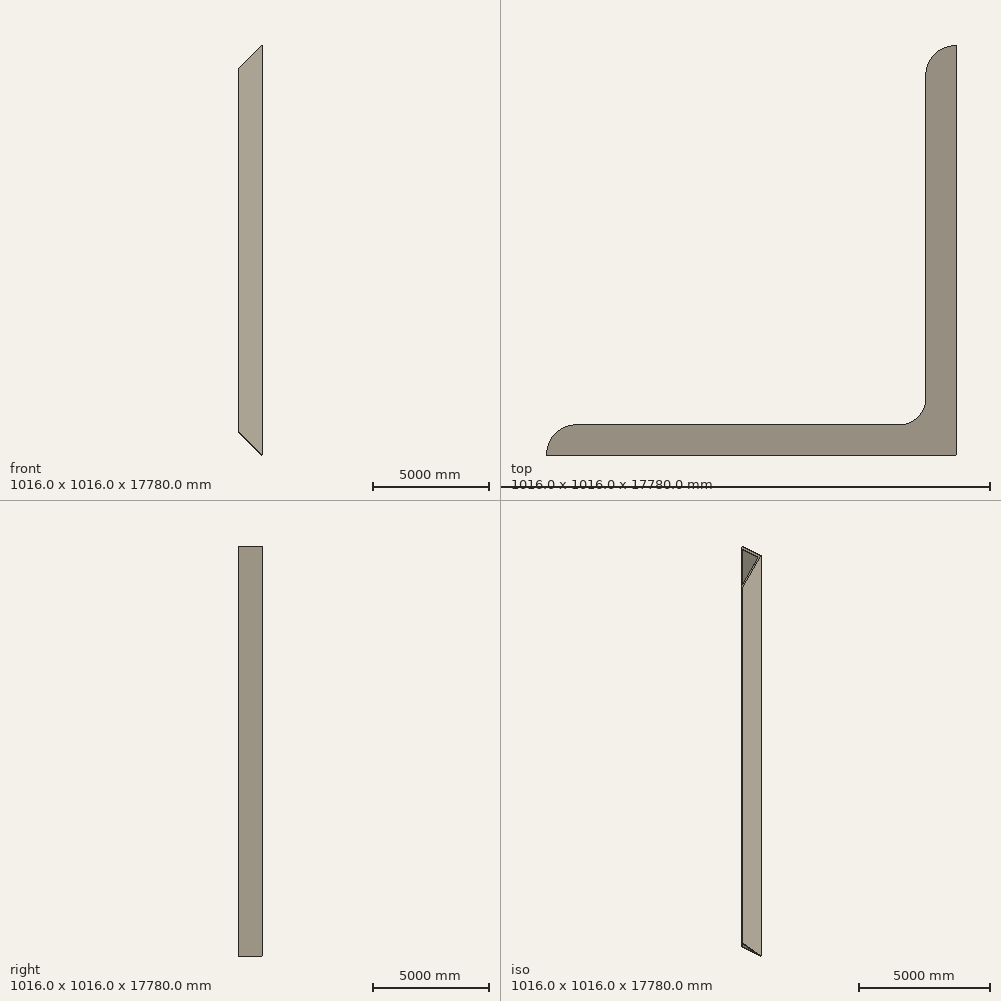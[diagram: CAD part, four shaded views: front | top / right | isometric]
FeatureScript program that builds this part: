
annotation { "Feature Type Name" : "Feature", "Feature Type Description" : "" }
export const myFeature = defineFeature(function(context is Context, id is Id, definition is map)
    precondition{}
    {
        {
            var Q0;
            Q0=qCreatedBy(makeId("Top.planeOp"),FACE);
            var sketch = newSketch(context, id + "F0", { "sketchPlane" : qUnion([Q0])});
            skLineSegment(sketch, "E0", {"start": v(0, 0) * mm, "end": v(1016, 0) * mm});
            skLineSegment(sketch, "E1", {"start": v(1016, 0) * mm, "end": v(1016, 1016) * mm});
            skLineSegment(sketch, "E2", {"start": v(939.8, 939.8) * mm, "end": v(939.8, 139.7) * mm});
            skLineSegment(sketch, "E3", {"start": v(876.3, 76.2) * mm, "end": v(76.2, 76.2) * mm});
            skArc(sketch, "E4", {"start": v(0, 0) * mm, "mid": v(22.32, 53.88) * mm, "end": v(76.2, 76.2) * mm});
            skArc(sketch, "E5", {"start": v(939.8, 939.8) * mm, "mid": v(962.12, 993.68) * mm, "end": v(1016, 1016) * mm});
            skPoint(sketch, "E6.visualSharp", {"position": v(939.8, 76.2) * mm});
            skArc(sketch, "E6.filletArc", {"start": v(876.3, 76.2) * mm, "mid": v(921.2, 94.8) * mm, "end": v(939.8, 139.7) * mm});
            skSolve(sketch);
        }
        {
            var Q0;
            Q0 = qSketchRegion(id + "F0", true);
            extrude(context, id + "F1", {"entities" : qUnion([Q0]), "depth" : 17780 * mm, "offsetDistance" : 25.4 * mm});
        }
        {
            var Q0;
            Q0=makeQuery(id+"F1.opExtrude","SWEPT_FACE",FACE,{"disambiguationData":[OSD([sQuery(id+"F0.wireOp",EDGE,"E0")])]});
            var sketch = newSketch(context, id + "F2", { "sketchPlane" : qUnion([Q0])});
            skLineSegment(sketch, "E7", {"start": v(1016, 17780) * mm, "end": v(-530.7, 16233.3) * mm});
            skLineSegment(sketch, "E8", {"start": v(-530.7, 16233.3) * mm, "end": v(-822.01, 18363) * mm});
            skLineSegment(sketch, "E9", {"start": v(-822.01, 18363) * mm, "end": v(1016, 17780) * mm});
            skLineSegment(sketch, "E10", {"start": v(1016, 0) * mm, "end": v(-799.1, 1815.1) * mm});
            skLineSegment(sketch, "E11", {"start": v(-799.1, 1815.1) * mm, "end": v(-1083.24, -1495.06) * mm});
            skLineSegment(sketch, "E12", {"start": v(-1083.24, -1495.06) * mm, "end": v(1016, 0) * mm});
            skSolve(sketch);
        }
        {
            var Q0;
            {var subQ1=sQuery(id+"F0.wireOp",EDGE,"E0");var subQ2=makeQuery(id+"F1.opExtrude","CAP_EDGE",EDGE,{"disambiguationData":[OSD([subQ1])],"isStart":false});Q0=makeQuery(id+"F2.imprint","IMPRINT",FACE,{"disambiguationData":[TD([[makeQuery(id+"F2.imprint","IMPRINT",EDGE,{"derivedFrom":subQ2}),-1.0]])]});}
            var Q1;
            {var subQ1=sQuery(id+"F0.wireOp",EDGE,"E0");var subQ2=makeQuery(id+"F1.opExtrude","CAP_EDGE",EDGE,{"disambiguationData":[OSD([subQ1])],"isStart":true});Q1=makeQuery(id+"F2.imprint","IMPRINT",FACE,{"disambiguationData":[TD([[makeQuery(id+"F2.imprint","IMPRINT",EDGE,{"derivedFrom":subQ2}),1.0]])]});}
            extrude(context, id + "F3", {"entities" : qUnion([Q0, Q1]), "operationType" : NewBodyOperationType.REMOVE, "endBound" : BoundingType.THROUGH_ALL, "oppositeDirection" : true, "depth" : 25.4 * mm, "offsetDistance" : 25.4 * mm});
        }
    });
